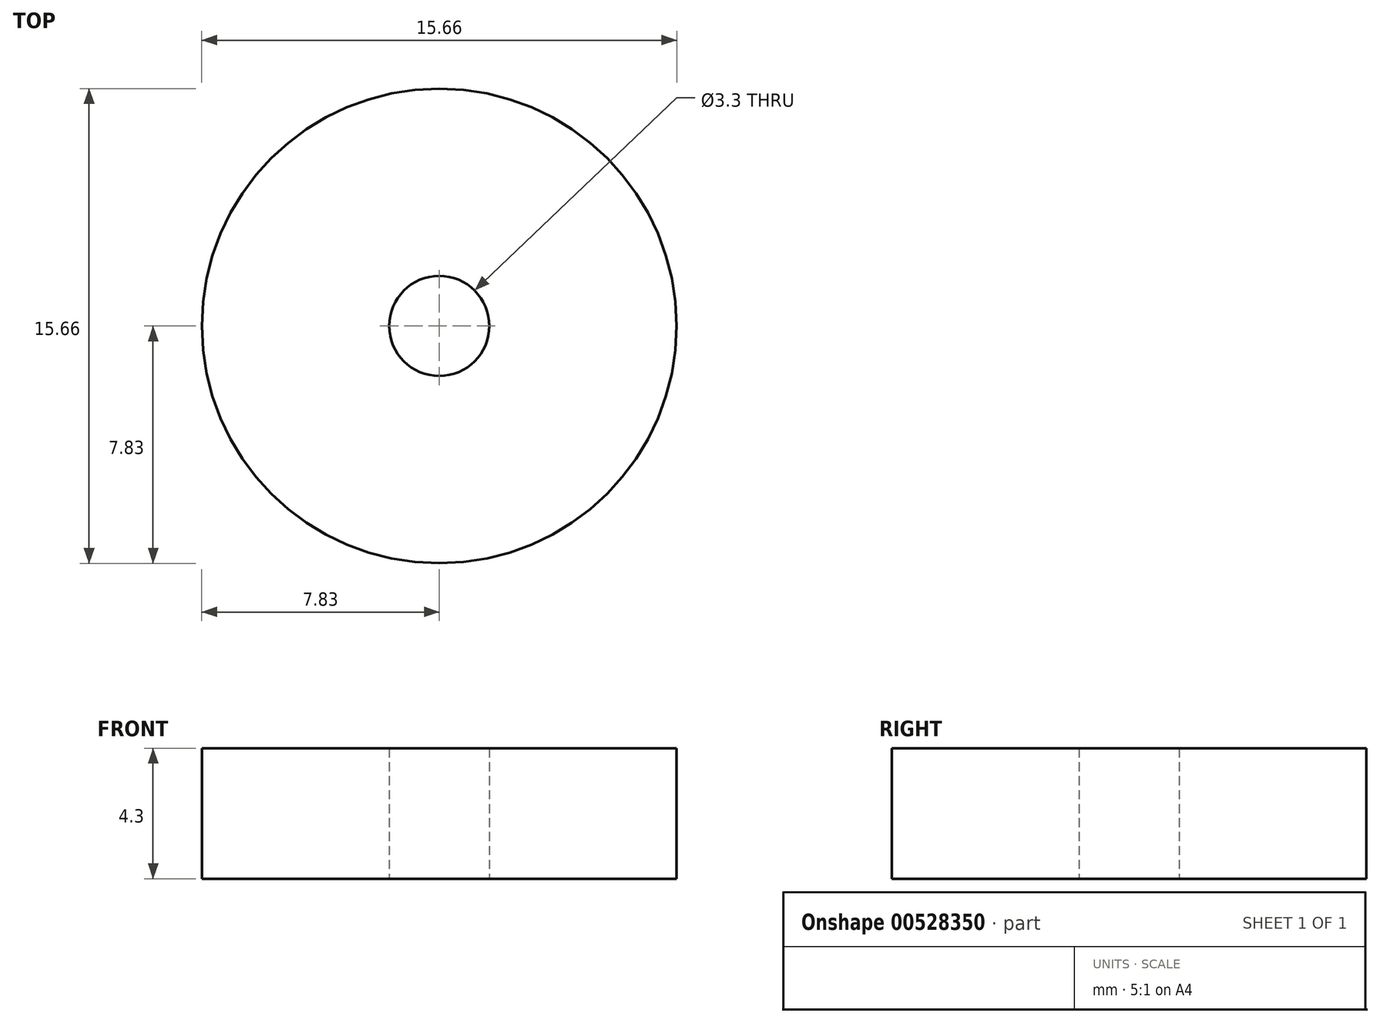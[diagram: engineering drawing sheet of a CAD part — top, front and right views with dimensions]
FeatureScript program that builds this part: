
annotation { "Feature Type Name" : "Feature", "Feature Type Description" : "" }
export const myFeature = defineFeature(function(context is Context, id is Id, definition is map)
    precondition{}
    {
        {
            var Q0;
            Q0=qCreatedBy(makeId("Top.planeOp"),FACE);
            var sketch = newSketch(context, id + "F0", { "sketchPlane" : qUnion([Q0])});
            skCircle(sketch, "E0", {"center": v(0, 0) * mm, "radius": 7.83 * mm});
            skCircle(sketch, "E1", {"center": v(0, 0) * mm, "radius": 1.65 * mm});
            skSolve(sketch);
        }
        {
            var Q0;
            Q0 = qSketchRegion(id + "F0", true);
            extrude(context, id + "F1", {"entities" : qUnion([Q0]), "depth" : 4.3 * mm, "offsetDistance" : 25 * mm});
        }
        {
            var Q0;
            Q0=makeQuery(id+"F1.opExtrude","CAP_FACE",FACE,{"disambiguationData":[OSD([sQuery(id+"F0.wireOp",EDGE,"E0")])],"isStart":false});
            var sketch = newSketch(context, id + "F2", { "sketchPlane" : qUnion([Q0])});
            skCircle(sketch, "E2", {"center": v(0, 0) * mm, "radius": 1.6 * mm});
            skSolve(sketch);
        }
        {
            var Q0;
            Q0 = qSketchRegion(id + "F2", true);
            extrude(context, id + "F3", {"entities" : qUnion([Q0]), "operationType" : NewBodyOperationType.REMOVE, "oppositeDirection" : true, "depth" : 25 * mm, "offsetDistance" : 25 * mm});
        }
    });
